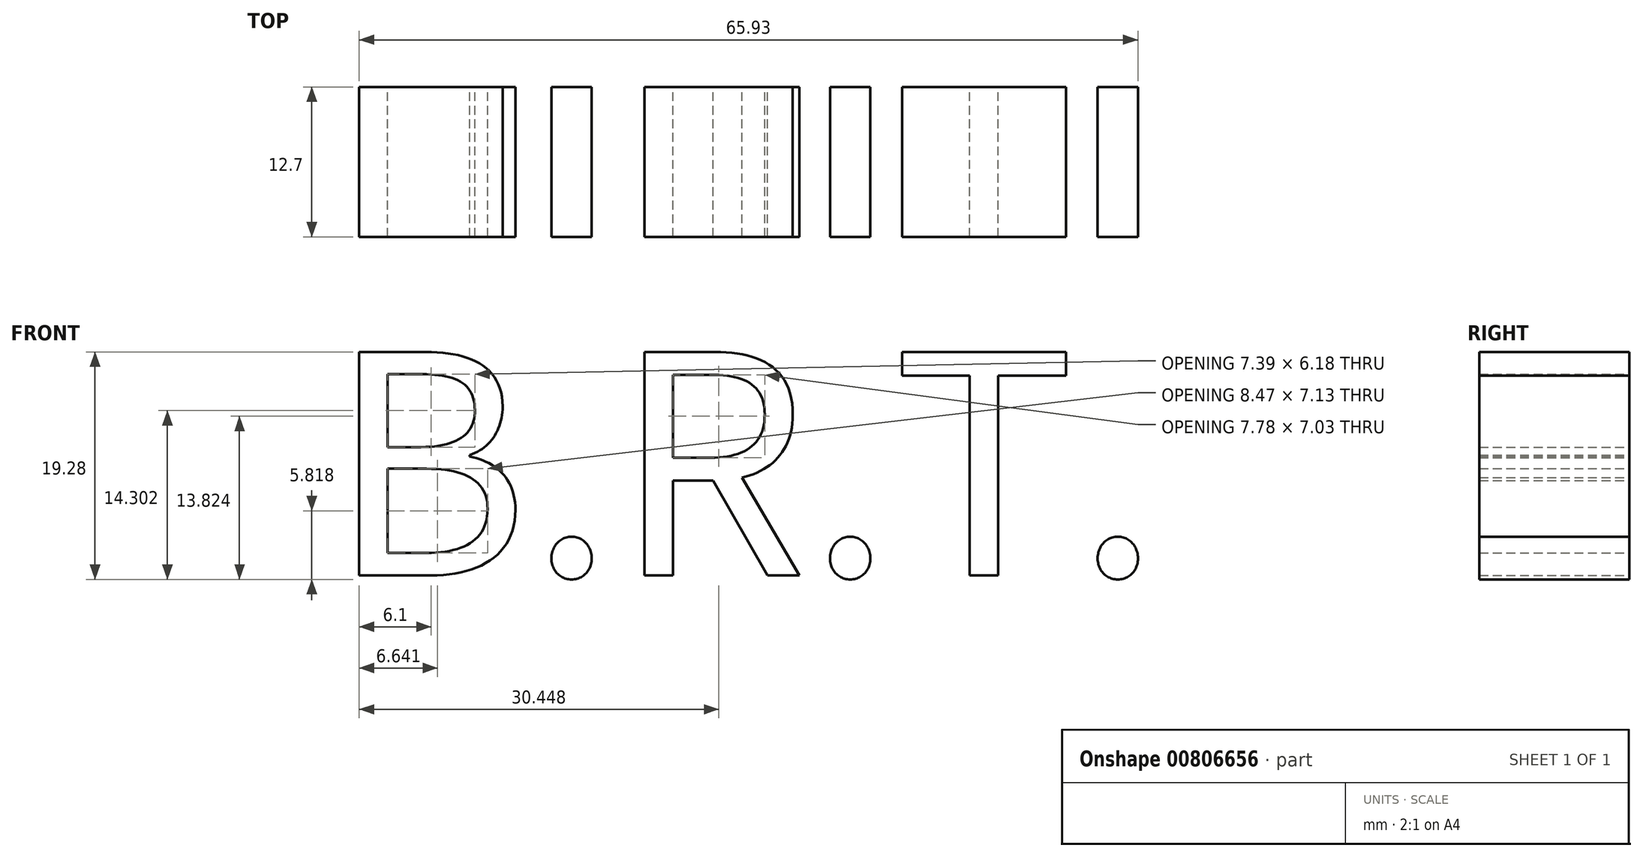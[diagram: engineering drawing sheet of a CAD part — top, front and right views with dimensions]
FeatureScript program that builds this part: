
annotation { "Feature Type Name" : "Feature", "Feature Type Description" : "" }
export const myFeature = defineFeature(function(context is Context, id is Id, definition is map)
    precondition{}
    {
        {
            var Q0;
            Q0=qCreatedBy(makeId("Front.planeOp"),FACE);
            var sketch = newSketch(context, id + "F0", { "sketchPlane" : qUnion([Q0])});
            skText(sketch, "E0", { "text": "B.R.T.", "fontName": "NotoSansCJKkr-Regular.otf"});
            const initialGuessF0  = {"E0": [-0.04271, 0.04138, 1, 0, 0.0186]};
            skSetInitialGuess(sketch, initialGuessF0);
            skSolve(sketch);
        }
        {
            var Q0;
            Q0 = qSketchRegion(id + "F0", true);
            extrude(context, id + "F1", {"entities" : qUnion([Q0]), "depth" : 12.7 * mm, "offsetDistance" : 25.4 * mm});
        }
    });
